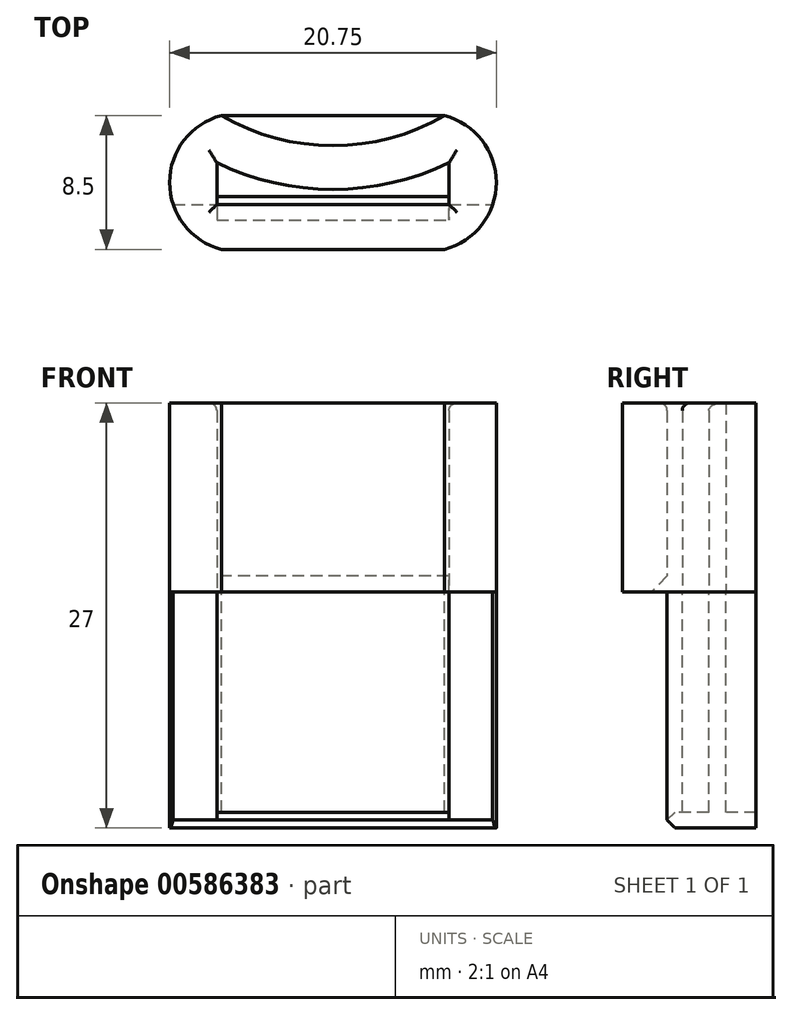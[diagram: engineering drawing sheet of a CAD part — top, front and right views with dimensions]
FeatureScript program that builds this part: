
annotation { "Feature Type Name" : "Feature", "Feature Type Description" : "" }
export const myFeature = defineFeature(function(context is Context, id is Id, definition is map)
    precondition{}
    {
        {
            var Q0;
            Q0=qCreatedBy(makeId("Top.planeOp"),FACE);
            var sketch = newSketch(context, id + "F0", { "sketchPlane" : qUnion([Q0])});
            skLineSegment(sketch, "E0.bottom", {"start": v(2.14, 3) * mm, "end": v(2.42, 3) * mm});
            skLineSegment(sketch, "E0.top", {"start": v(2.42, -5.5) * mm, "end": v(16.6, -5.5) * mm});
            skLineSegment(sketch, "E1.top", {"start": v(2.14, -2.65) * mm, "end": v(16.89, -2.65) * mm});
            skLineSegment(sketch, "E1.left", {"start": v(2.14, 0) * mm, "end": v(2.14, -2.65) * mm});
            skLineSegment(sketch, "E1.right", {"start": v(16.89, 0) * mm, "end": v(16.89, -2.65) * mm});
            skPoint(sketch, "E2.start.orphan", {"position": v(2.14, 3) * mm});
            skPoint(sketch, "E3.end.orphan", {"position": v(2.14, -1.25) * mm});
            skPoint(sketch, "E3.start.orphan", {"position": v(-0.86, -1.25) * mm});
            skPoint(sketch, "E4.end.orphan", {"position": v(9.51, -2.65) * mm});
            skPoint(sketch, "E4.start.orphan", {"position": v(9.51, -5.5) * mm});
            skPoint(sketch, "E5.end.orphan", {"position": v(16.89, -1.25) * mm});
            skPoint(sketch, "E5.start.orphan", {"position": v(19.89, -1.25) * mm});
            skArc(sketch, "E6", {"start": v(2.14, 0) * mm, "mid": v(9.51, -1.7) * mm, "end": v(16.89, 0) * mm});
            skLineSegment(sketch, "E7", {"start": v(2.14, -2.65) * mm, "end": v(4.64, -2.65) * mm});
            skArc(sketch, "E8", {"start": v(2.42, 3) * mm, "mid": v(-0.86, -1.25) * mm, "end": v(2.42, -5.5) * mm});
            skArc(sketch, "E9.MirrorCS", {"start": v(16.6, 3) * mm, "mid": v(19.89, -1.25) * mm, "end": v(16.6, -5.5) * mm});
            skPoint(sketch, "E10.orphan", {"position": v(9.51, 3) * mm});
            skPoint(sketch, "E11.orphan", {"position": v(-0.86, 3) * mm});
            skPoint(sketch, "E12.orphan", {"position": v(19.89, -5.5) * mm});
            skPoint(sketch, "E0.right.start.orphan", {"position": v(19.89, 3) * mm});
            skPoint(sketch, "E0.left.end.orphan", {"position": v(-0.86, -5.5) * mm});
            skPoint(sketch, "E13.orphan", {"position": v(4.64, -5.5) * mm});
            skPoint(sketch, "E14.orphan", {"position": v(4.64, 3) * mm});
            skArc(sketch, "E15", {"start": v(2.42, 3) * mm, "mid": v(9.51, 1.09) * mm, "end": v(16.6, 3) * mm});
            skSolve(sketch);
        }
        {
            var Q0;
            Q0 = qSketchRegion(id + "F0", true);
            extrude(context, id + "F1", {"entities" : qUnion([Q0]), "depth" : 12 * mm, "offsetDistance" : 25.4 * mm});
        }
        {
            var Q0;
            Q0=makeQuery(id+"F1.opExtrude","CAP_FACE",FACE,{"disambiguationData":[OSD([sQuery(id+"F0.wireOp",EDGE,"E0.top"),sQuery(id+"F0.wireOp",EDGE,"E1.top"),sQuery(id+"F0.wireOp",EDGE,"E1.left"),sQuery(id+"F0.wireOp",EDGE,"E1.right"),sQuery(id+"F0.wireOp",EDGE,"E6"),sQuery(id+"F0.wireOp",EDGE,"E7"),sQuery(id+"F0.wireOp",EDGE,"E8"),sQuery(id+"F0.wireOp",EDGE,"E9.MirrorCS"),sQuery(id+"F0.wireOp",EDGE,"E15")])],"isStart":true});
            var sketch = newSketch(context, id + "F2", { "sketchPlane" : qUnion([Q0])});
            skArc(sketch, "E16.0", {"start": v(2.42, -3) * mm, "mid": v(9.51, -1.09) * mm, "end": v(16.6, -3) * mm});
            skPoint(sketch, "E17.orphan", {"position": v(16.6, 5.5) * mm});
            skPoint(sketch, "E18.orphan", {"position": v(2.42, 5.5) * mm});
            skArc(sketch, "E19.0", {"start": v(2.14, 0) * mm, "mid": v(9.51, 1.7) * mm, "end": v(16.89, 0) * mm});
            skLineSegment(sketch, "E20.0", {"start": v(16.89, 0) * mm, "end": v(16.89, 2.65) * mm});
            skLineSegment(sketch, "E21.0", {"start": v(2.14, 0) * mm, "end": v(2.14, 2.65) * mm});
            skPoint(sketch, "E22.orphan", {"position": v(-0.63, 2.65) * mm});
            skLineSegment(sketch, "E23", {"start": v(-0.63, 2.65) * mm, "end": v(2.14, 2.65) * mm});
            skLineSegment(sketch, "E24.trimOffspring", {"start": v(16.89, 2.65) * mm, "end": v(19.66, 2.65) * mm});
            skPoint(sketch, "E25.0.end.orphan", {"position": v(19.89, 1.25) * mm});
            skArc(sketch, "E26.0", {"start": v(2.42, -3) * mm, "mid": v(-0.33, -0.84) * mm, "end": v(-0.63, 2.65) * mm});
            skArc(sketch, "E27.0", {"start": v(16.6, -3) * mm, "mid": v(19.36, -0.84) * mm, "end": v(19.66, 2.65) * mm});
            skSolve(sketch);
        }
        {
            var Q0;
            Q0 = qSketchRegion(id + "F2", true);
            extrude(context, id + "F3", {"entities" : qUnion([Q0]), "depth" : 14 * mm, "offsetDistance" : 25.4 * mm});
        }
        {
            var Q0;
            Q0=makeQuery(id+"F3.opExtrude","CAP_FACE",FACE,{"disambiguationData":[OSD([sQuery(id+"F2.wireOp",EDGE,"E16.0"),sQuery(id+"F2.wireOp",EDGE,"E19.0"),sQuery(id+"F2.wireOp",EDGE,"E20.0"),sQuery(id+"F2.wireOp",EDGE,"E21.0"),sQuery(id+"F2.wireOp",EDGE,"E23"),sQuery(id+"F2.wireOp",EDGE,"E24.trimOffspring"),sQuery(id+"F2.wireOp",EDGE,"E26.0"),sQuery(id+"F2.wireOp",EDGE,"E27.0")])],"isStart":false});
            var sketch = newSketch(context, id + "F4", { "sketchPlane" : qUnion([Q0])});
            skArc(sketch, "E28.0", {"start": v(2.42, -3) * mm, "mid": v(-0.33, -0.84) * mm, "end": v(-0.63, 2.65) * mm});
            skArc(sketch, "E29.0", {"start": v(16.6, -3) * mm, "mid": v(19.36, -0.84) * mm, "end": v(19.66, 2.65) * mm});
            skLineSegment(sketch, "E30", {"start": v(2.42, -3) * mm, "end": v(16.6, -3) * mm});
            skLineSegment(sketch, "E31", {"start": v(-0.63, 2.65) * mm, "end": v(19.66, 2.65) * mm});
            skSolve(sketch);
        }
        {
            var Q0;
            Q0 = qSketchRegion(id + "F4", true);
            extrude(context, id + "F5", {"entities" : qUnion([Q0]), "operationType" : NewBodyOperationType.ADD, "depth" : 1 * mm, "offsetDistance" : 25.4 * mm});
        }
        {
            var Q0;
            Q0=makeQuery(id+"F5.opExtrude","CAP_EDGE",EDGE,{"disambiguationData":[OSD([sQuery(id+"F4.wireOp",EDGE,"E31")])],"isStart":false});
            chamfer(context, id + "F6", {"entities" : qUnion([Q0]), "width" : 0.5 * mm, "tangentPropagation" : true});
        }
        {
            var Q0;
            Q0=makeQuery(id+"F1.opExtrude","CAP_EDGE",EDGE,{"disambiguationData":[OSD([sQuery(id+"F0.wireOp",EDGE,"E1.top"),sQuery(id+"F0.wireOp",EDGE,"E7")])],"isStart":true});
            chamfer(context, id + "F7", {"entities" : qUnion([Q0]), "width" : 1 * mm, "tangentPropagation" : true});
        }
        {
            var Q0;
            Q0=makeQuery(id+"F5.opExtrude","CAP_EDGE",EDGE,{"disambiguationData":[OSD([sQuery(id+"F4.wireOp",EDGE,"E31")])],"isStart":true});
            chamfer(context, id + "F8", {"entities" : qUnion([Q0]), "width" : 0.5 * mm, "tangentPropagation" : true});
        }
        {
            var Q0;
            Q0=makeQuery(id+"F1.opExtrude","CAP_EDGE",EDGE,{"disambiguationData":[OSD([sQuery(id+"F0.wireOp",EDGE,"E1.top"),sQuery(id+"F0.wireOp",EDGE,"E7")])],"isStart":false});
            var Q1;
            Q1=makeQuery(id+"F1.opExtrude","CAP_EDGE",EDGE,{"disambiguationData":[OSD([sQuery(id+"F0.wireOp",EDGE,"E1.left")])],"isStart":false});
            var Q2;
            Q2=makeQuery(id+"F1.opExtrude","CAP_EDGE",EDGE,{"disambiguationData":[OSD([sQuery(id+"F0.wireOp",EDGE,"E6")])],"isStart":false});
            var Q3;
            Q3=makeQuery(id+"F1.opExtrude","CAP_EDGE",EDGE,{"disambiguationData":[OSD([sQuery(id+"F0.wireOp",EDGE,"E1.right")])],"isStart":false});
            fillet(context, id + "F9", {"entities" : qUnion([Q0, Q1, Q2, Q3]), "radius" : 0.5 * mm, "tangentPropagation" : true, "allowEdgeOverflow" : false});
        }
    });
